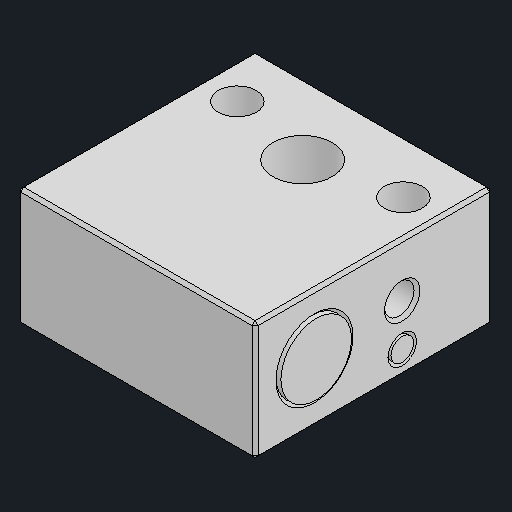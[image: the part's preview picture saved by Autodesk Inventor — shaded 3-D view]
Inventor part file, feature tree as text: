
AUTODESK INVENTOR PART (.ipt)
format: ipt  version: 2024.2 (Build 282272000, 272)  size: 154,112 bytes
history: native  units: mm
features: other x5, chamfer x1
ambient origin geometry x8: Origin, YZ Plane, XZ Plane, XY Plane, X Axis, Y Axis, Z Axis, Center Point
bodies: Body1 (feature_tree), Body2 (feature_tree), Body3 (feature_tree)
feature tree (6):
  other  "솔리드1"
  other  "솔리드2"
  other  "솔리드3"
  chamfer  "Chamfer2"  [1 undecoded]
  other  "Dome2"
  other  "Boss-Extrude3"
note: 1 required parameter value undecoded (feature->parameter linkage not recoverable at this tier; creation-order binding heuristic only, values carry confidence <= 0.55)
